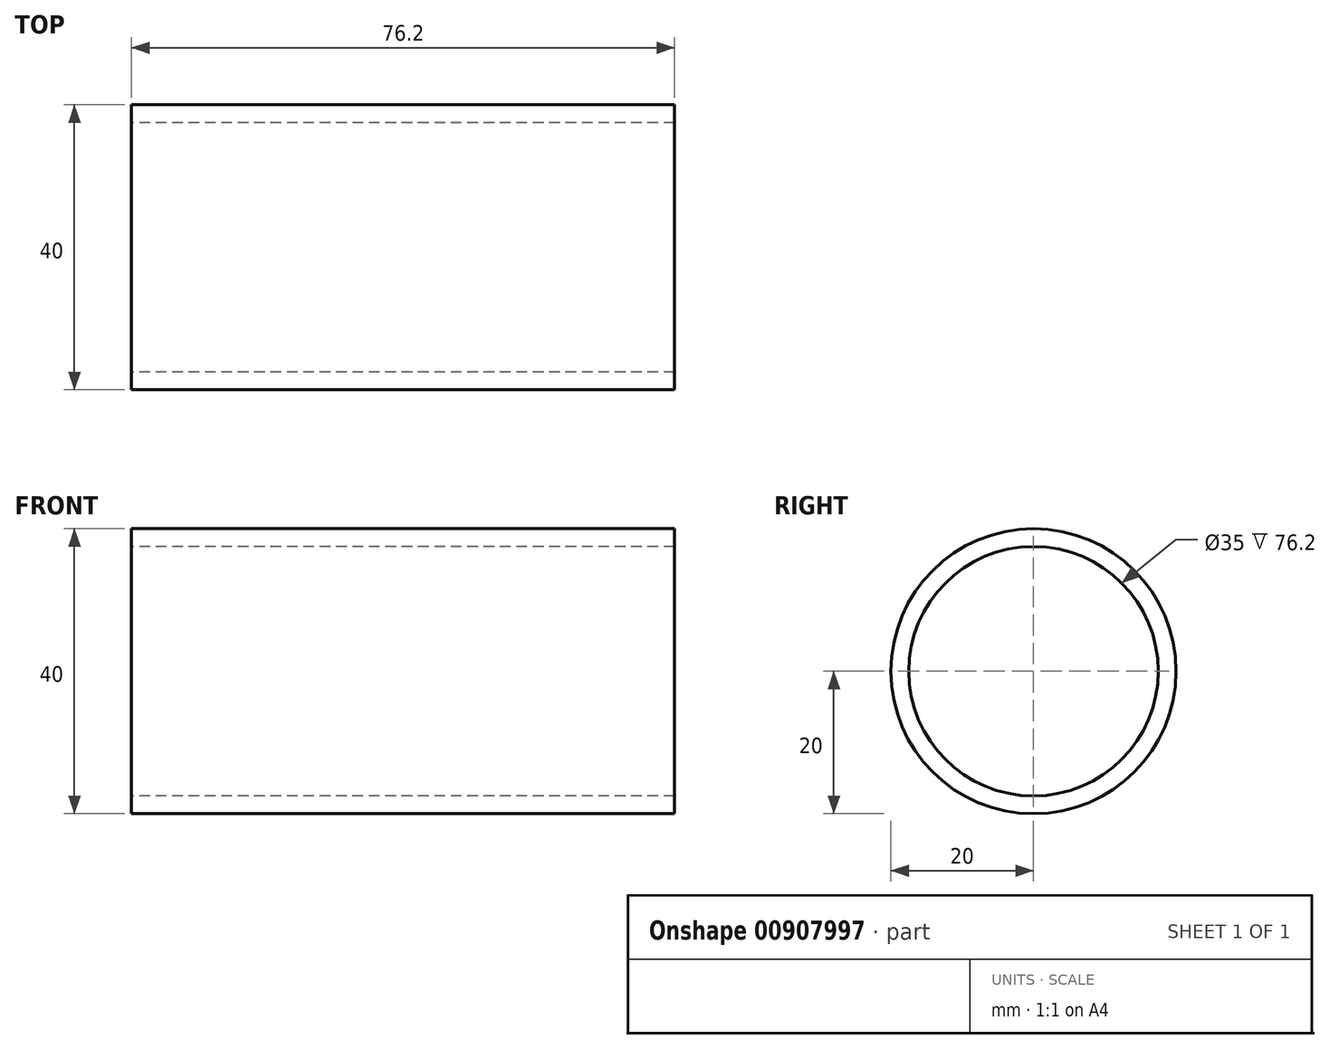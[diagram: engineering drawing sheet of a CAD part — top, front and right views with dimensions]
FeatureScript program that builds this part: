
annotation { "Feature Type Name" : "Feature", "Feature Type Description" : "" }
export const myFeature = defineFeature(function(context is Context, id is Id, definition is map)
    precondition{}
    {
        {
            var Q0;
            Q0=qCreatedBy(makeId("Right.planeOp"),FACE);
            var sketch = newSketch(context, id + "F0", { "sketchPlane" : qUnion([Q0])});
            skCircle(sketch, "E0", {"center": v(0, 0) * mm, "radius": 20 * mm});
            skCircle(sketch, "E1.0", {"center": v(0, 0) * mm, "radius": 17.5 * mm});
            skSolve(sketch);
        }
        {
            var Q0;
            Q0 = qSketchRegion(id + "F0", true);
            extrude(context, id + "F1", {"entities" : qUnion([Q0]), "depth" : 76.2 * mm, "offsetDistance" : 25.4 * mm});
        }
    });
